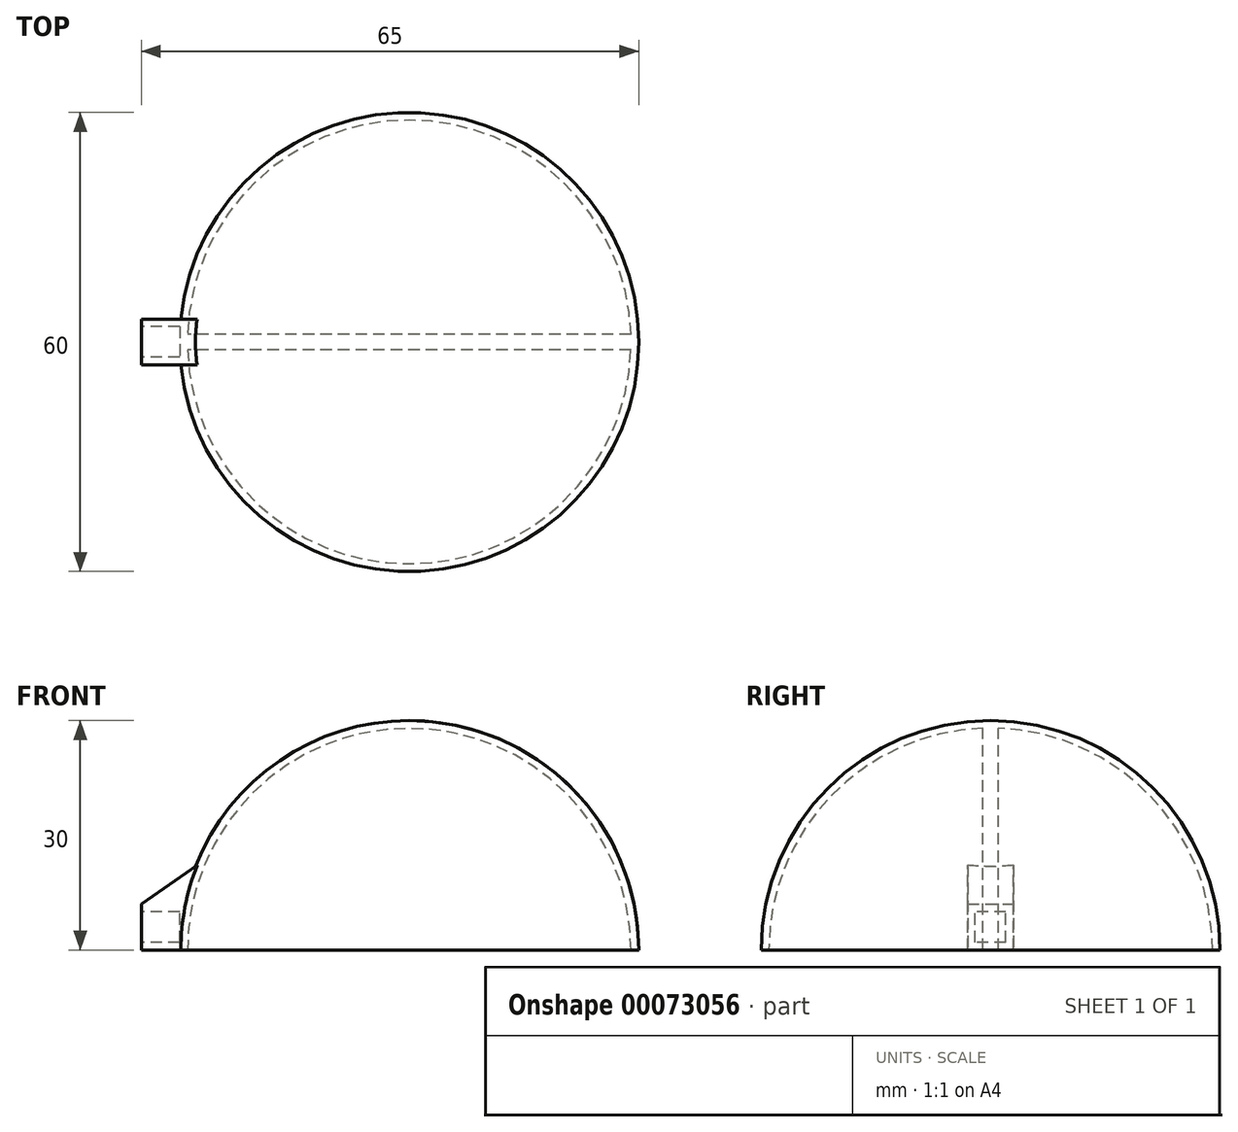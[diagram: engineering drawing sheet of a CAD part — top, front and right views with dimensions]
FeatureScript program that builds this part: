
annotation { "Feature Type Name" : "Feature", "Feature Type Description" : "" }
export const myFeature = defineFeature(function(context is Context, id is Id, definition is map)
    precondition{}
    {
        {
            var Q0;
            Q0=qCreatedBy(makeId("Front.planeOp"),FACE);
            var sketch = newSketch(context, id + "F3", { "sketchPlane" : qUnion([Q0])});
            skArc(sketch, "E0", {"start": v(30, 0) * mm, "mid": v(21.21, 21.21) * mm, "end": v(0, 30) * mm});
            skArc(sketch, "E1", {"start": v(29, 0) * mm, "mid": v(20.5, 20.5) * mm, "end": v(0, 29) * mm});
            skLineSegment(sketch, "E2", {"start": v(30, 0) * mm, "end": v(29, 0) * mm});
            skLineSegment(sketch, "E3", {"start": v(0, 28.09) * mm, "end": v(0, -26.06) * mm, "construction": true});
            skLineSegment(sketch, "E4", {"start": v(0, 30) * mm, "end": v(0, 29) * mm});
            skSolve(sketch);
        }
        {
            var Q0;
            Q0=makeQuery(id+"F3.imprint","IMPRINT",FACE,{"disambiguationData":[TD([[makeQuery(id+"F3.imprint","IMPRINT",EDGE,{"derivedFrom":sQuery(id+"F3.wireOp",EDGE,"E0")}),1.0]])]});
            var Q1;
            Q1=sQuery(id+"F3.wireOp",EDGE,"E0");
            var Q2;
            Q2=sQuery(id+"F3.wireOp",EDGE,"E2");
            var Q3;
            Q3=sQuery(id+"F3.wireOp",EDGE,"E1");
            var Q4;
            Q4=sQuery(id+"F3.wireOp",EDGE,"E3");
            revolve(context, id + "F4", {"entities" : qUnion([Q0]), "surfaceEntities" : qUnion([Q1, Q2, Q3]), "axis" : qUnion([Q4]), "revolveType" : RevolveType.FULL});
        }
        {
            var Q0;
            Q0=qCreatedBy(makeId("Front.planeOp"),FACE);
            var sketch = newSketch(context, id + "F0", { "sketchPlane" : qUnion([Q0])});
            skArc(sketch, "E5", {"start": v(29, 0) * mm, "mid": v(0, 29) * mm, "end": v(-29, 0) * mm});
            skLineSegment(sketch, "E6", {"start": v(29, 0) * mm, "end": v(-29, 0) * mm});
            skSolve(sketch);
        }
        {
            var Q0;
            Q0=makeQuery(id+"F0.imprint","IMPRINT",FACE,{"disambiguationData":[TD([[makeQuery(id+"F0.imprint","IMPRINT",EDGE,{"derivedFrom":sQuery(id+"F0.wireOp",EDGE,"E5")}),1.0]])]});
            var Q1;
            Q1=sQuery(id+"F0.wireOp",EDGE,"E5");
            var Q2;
            Q2=sQuery(id+"F0.wireOp",EDGE,"E6");
            extrude(context, id + "F5", {"entities" : qUnion([Q0]), "operationType" : NewBodyOperationType.ADD, "surfaceEntities" : qUnion([Q1, Q2]), "depth" : 1 * mm, "hasSecondDirection" : true, "secondDirectionOppositeDirection" : true, "secondDirectionDepth" : 1 * mm});
        }
        {
            var Q0;
            Q0=qCreatedBy(makeId("Front.planeOp"),FACE);
            var sketch = newSketch(context, id + "F6", { "sketchPlane" : qUnion([Q0])});
            skLineSegment(sketch, "E7", {"start": v(-29, 0) * mm, "end": v(-35, 0) * mm});
            skLineSegment(sketch, "E8", {"start": v(-35, 0) * mm, "end": v(-35, 6) * mm});
            skLineSegment(sketch, "E9", {"start": v(-35, 6) * mm, "end": v(-26.4, 12) * mm});
            skArc(sketch, "E10", {"start": v(-26.4, 12) * mm, "mid": v(-28.34, 6.14) * mm, "end": v(-29, 0) * mm});
            skSolve(sketch);
        }
        {
            var Q0;
            {var subQ0=sQuery(id+"F6.wireOp",EDGE,"E8");Q0=makeQuery(id+"F6.imprint","IMPRINT",FACE,{"disambiguationData":[TD([[makeQuery(id+"F6.imprint","IMPRINT",EDGE,{"derivedFrom":subQ0}),-1.0]])]});}
            extrude(context, id + "F1", {"entities" : qUnion([Q0]), "operationType" : NewBodyOperationType.ADD, "depth" : 3 * mm, "hasSecondDirection" : true, "secondDirectionOppositeDirection" : true, "secondDirectionDepth" : 3 * mm});
        }
        {
            var Q0;
            Q0=makeQuery(id+"F1.opExtrude","SWEPT_FACE",FACE,{"disambiguationData":[OSD([sQuery(id+"F6.wireOp",EDGE,"E8")])]});
            var sketch = newSketch(context, id + "F2", { "sketchPlane" : qUnion([Q0])});
            skLineSegment(sketch, "E11.bottom", {"start": v(-2, 1) * mm, "end": v(2, 1) * mm});
            skLineSegment(sketch, "E11.top", {"start": v(-2, 5) * mm, "end": v(2, 5) * mm});
            skLineSegment(sketch, "E11.left", {"start": v(-2, 1) * mm, "end": v(-2, 5) * mm});
            skLineSegment(sketch, "E11.right", {"start": v(2, 1) * mm, "end": v(2, 5) * mm});
            skSolve(sketch);
        }
        {
            var Q0;
            Q0=makeQuery(id+"F2.imprint","IMPRINT",FACE,{"disambiguationData":[TD([[makeQuery(id+"F2.imprint","IMPRINT",EDGE,{"derivedFrom":sQuery(id+"F2.wireOp",EDGE,"E11.bottom")}),1.0]])]});
            extrude(context, id + "F7", {"entities" : qUnion([Q0]), "operationType" : NewBodyOperationType.REMOVE, "oppositeDirection" : true, "depth" : 5 * mm});
        }
    });
